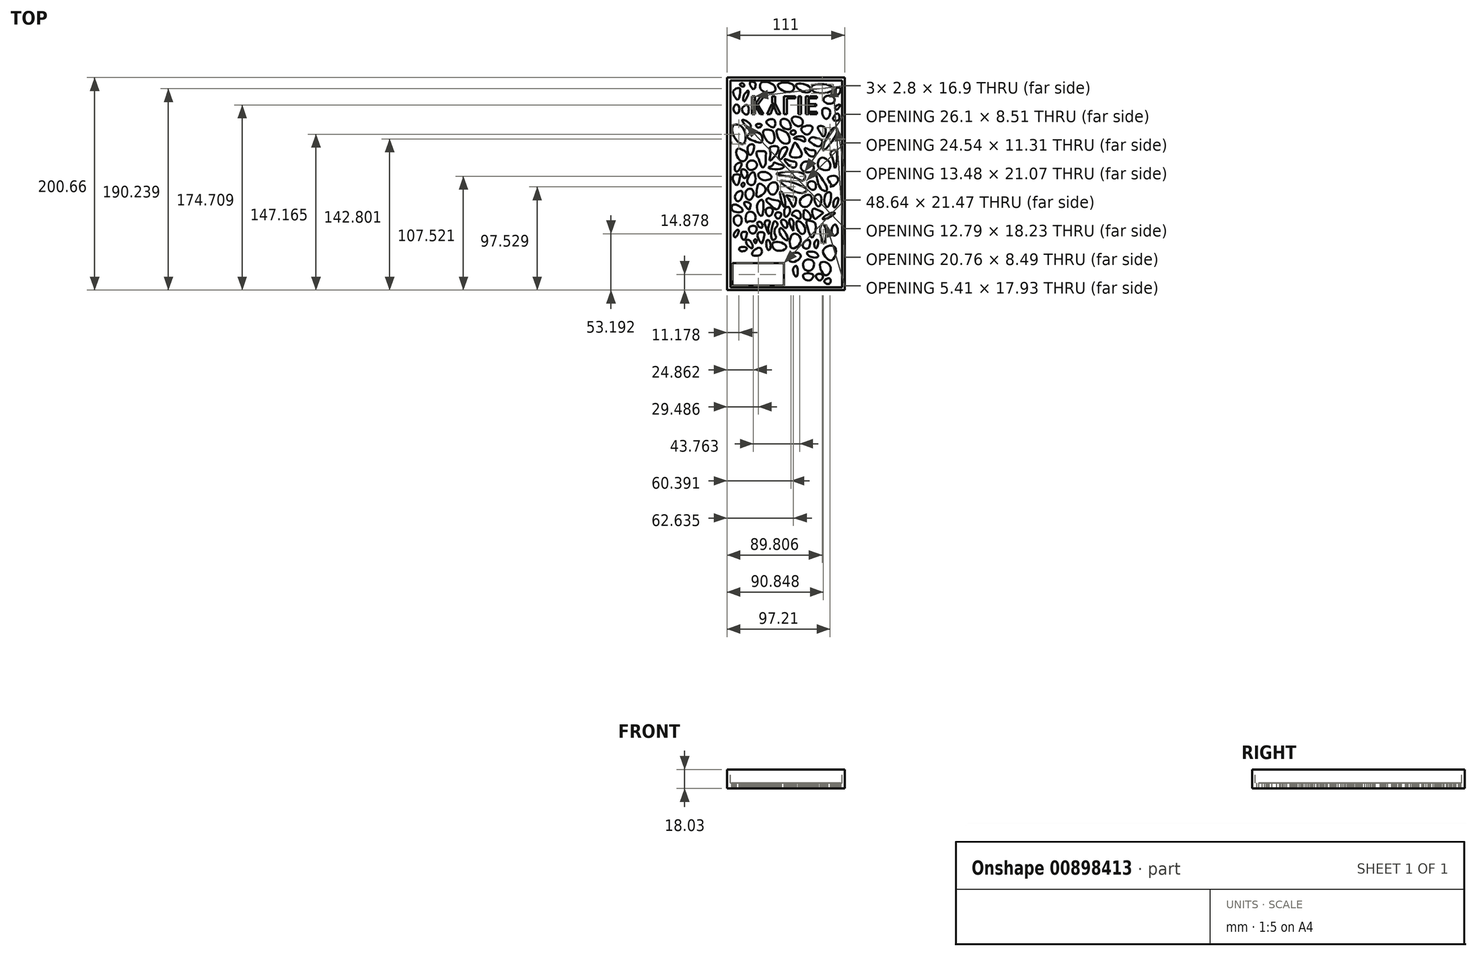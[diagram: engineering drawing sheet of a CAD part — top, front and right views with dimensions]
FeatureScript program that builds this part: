
annotation { "Feature Type Name" : "Feature", "Feature Type Description" : "" }
export const myFeature = defineFeature(function(context is Context, id is Id, definition is map)
    precondition{}
    {
        {
            var Q0;
            Q0=qCreatedBy(makeId("Top.planeOp"),FACE);
            var sketch = newSketch(context, id + "F0", { "sketchPlane" : qUnion([Q0])});
            skLineSegment(sketch, "E0.bottom", {"start": v(-57.32, 129.1) * mm, "end": v(53.68, 129.1) * mm});
            skLineSegment(sketch, "E0.top", {"start": v(-57.32, -71.56) * mm, "end": v(53.68, -71.56) * mm});
            skLineSegment(sketch, "E0.left", {"start": v(-57.32, 129.1) * mm, "end": v(-57.32, -71.56) * mm});
            skLineSegment(sketch, "E0.right", {"start": v(53.68, 129.1) * mm, "end": v(53.68, -71.56) * mm});
            skSolve(sketch);
        }
        {
            var Q0;
            Q0=makeQuery(id+"F0.imprint","IMPRINT",FACE,{"disambiguationData":[TD([[makeQuery(id+"F0.imprint","IMPRINT",EDGE,{"derivedFrom":sQuery(id+"F0.wireOp",EDGE,"E0.bottom")}),-1.0]])]});
            extrude(context, id + "F1", {"entities" : qUnion([Q0]), "depth" : 18.03 * mm, "offsetDistance" : 25.4 * mm});
        }
        {
            var Q0;
            Q0=makeQuery(id+"F1.opExtrude","CAP_FACE",FACE,{"disambiguationData":[OSD([sQuery(id+"F0.wireOp",EDGE,"E0.bottom"),sQuery(id+"F0.wireOp",EDGE,"E0.top"),sQuery(id+"F0.wireOp",EDGE,"E0.left"),sQuery(id+"F0.wireOp",EDGE,"E0.right")])],"isStart":false});
            var sketch = newSketch(context, id + "F2", { "sketchPlane" : qUnion([Q0])});
            skLineSegment(sketch, "E1.bottom", {"start": v(-54.27, 126.23) * mm, "end": v(51.3, 126.23) * mm});
            skLineSegment(sketch, "E1.top", {"start": v(-54.27, -68.92) * mm, "end": v(51.3, -68.92) * mm});
            skLineSegment(sketch, "E1.left", {"start": v(-54.27, 126.23) * mm, "end": v(-54.27, -68.92) * mm});
            skLineSegment(sketch, "E1.right", {"start": v(51.3, 126.23) * mm, "end": v(51.3, -68.92) * mm});
            skSolve(sketch);
        }
        {
            var Q0;
            Q0=makeQuery(id+"F2.imprint","IMPRINT",FACE,{"disambiguationData":[TD([[makeQuery(id+"F2.imprint","IMPRINT",EDGE,{"derivedFrom":sQuery(id+"F2.wireOp",EDGE,"E1.bottom")}),-1.0]])]});
            extrude(context, id + "F3", {"entities" : qUnion([Q0]), "operationType" : NewBodyOperationType.REMOVE, "oppositeDirection" : true, "depth" : 12.7 * mm, "offsetDistance" : 25.4 * mm});
        }
        {
            var Q0;
            Q0=makeQuery(id+"F1.opExtrude","CAP_FACE",FACE,{"disambiguationData":[OSD([sQuery(id+"F0.wireOp",EDGE,"E0.bottom"),sQuery(id+"F0.wireOp",EDGE,"E0.top"),sQuery(id+"F0.wireOp",EDGE,"E0.left"),sQuery(id+"F0.wireOp",EDGE,"E0.right")])],"isStart":true});
            var sketch = newSketch(context, id + "F4", { "sketchPlane" : qUnion([Q0])});
            skText(sketch, "E2", { "text": "KYLIE", "fontName": "AllertaStencil-Regular.ttf"});
            const initialGuessF4  = {"E2": [-0.03599, -0.1116, 1, 0, 0.01691]};
            skSetInitialGuess(sketch, initialGuessF4);
            skSolve(sketch);
        }
        {
            var Q0;
            Q0 = qSketchRegion(id + "F4", true);
            extrude(context, id + "F5", {"entities" : qUnion([Q0]), "operationType" : NewBodyOperationType.REMOVE, "oppositeDirection" : true, "depth" : 25.4 * mm, "offsetDistance" : 25.4 * mm});
        }
        {
            var Q0;
            Q0=makeQuery(id+"F1.opExtrude","CAP_FACE",FACE,{"disambiguationData":[OSD([sQuery(id+"F0.wireOp",EDGE,"E0.bottom"),sQuery(id+"F0.wireOp",EDGE,"E0.top"),sQuery(id+"F0.wireOp",EDGE,"E0.left"),sQuery(id+"F0.wireOp",EDGE,"E0.right")])],"isStart":true});
            var sketch = newSketch(context, id + "F6", { "sketchPlane" : qUnion([Q0])});
            skLineSegment(sketch, "E3.bottom", {"start": v(-52.16, 67.42) * mm, "end": v(-3.51, 67.42) * mm});
            skLineSegment(sketch, "E3.top", {"start": v(-52.16, 45.95) * mm, "end": v(-3.51, 45.95) * mm});
            skLineSegment(sketch, "E3.left", {"start": v(-52.16, 67.42) * mm, "end": v(-52.16, 45.95) * mm});
            skLineSegment(sketch, "E3.right", {"start": v(-3.51, 67.42) * mm, "end": v(-3.51, 45.95) * mm});
            skSolve(sketch);
        }
        {
            var Q0;
            Q0=makeQuery(id+"F6.imprint","IMPRINT",FACE,{"disambiguationData":[TD([[makeQuery(id+"F6.imprint","IMPRINT",EDGE,{"derivedFrom":sQuery(id+"F6.wireOp",EDGE,"E3.bottom")}),-1.0]])]});
            extrude(context, id + "F7", {"entities" : qUnion([Q0]), "operationType" : NewBodyOperationType.REMOVE, "oppositeDirection" : true, "depth" : 25.4 * mm, "offsetDistance" : 25.4 * mm});
        }
        {
            var Q0;
            Q0=makeQuery(id+"F1.opExtrude","CAP_FACE",FACE,{"disambiguationData":[OSD([sQuery(id+"F0.wireOp",EDGE,"E0.bottom"),sQuery(id+"F0.wireOp",EDGE,"E0.top"),sQuery(id+"F0.wireOp",EDGE,"E0.left"),sQuery(id+"F0.wireOp",EDGE,"E0.right")])],"isStart":true});
            var sketch = newSketch(context, id + "F8", { "sketchPlane" : qUnion([Q0])});
            skFitSpline(sketch, "E4", {"points": [v(-45.58, 33.96) * mm, v(-44.9, 31.22) * mm, v(-38.73, 31.9) * mm, v(-40.56, 34.41) * mm, v(-45.58, 33.96) * mm]});
            skFitSpline(sketch, "E5", {"points": [v(-33.47, 31.9) * mm, v(-38.73, 28.02) * mm, v(-38.73, 24.13) * mm, v(-35.07, 25.73) * mm, v(-33.47, 31.9) * mm]});
            skFitSpline(sketch, "E6", {"points": [v(-33.47, 38.07) * mm, v(-25.47, 37.84) * mm, v(-25.7, 31.9) * mm, v(-31.42, 33.73) * mm, v(-33.47, 38.07) * mm]});
            skFitSpline(sketch, "E7", {"points": [v(-33.47, 18.2) * mm, v(-36.67, 12.93) * mm, v(-30.73, 11.1) * mm, v(-29.59, 15.22) * mm, v(-33.47, 18.2) * mm]});
            skFitSpline(sketch, "E8", {"points": [v(-24.79, 27.33) * mm, v(-28.67, 19.79) * mm, v(-26.62, 17.05) * mm, v(-22.27, 17.73) * mm, v(-23.19, 24.13) * mm, v(-24.79, 27.33) * mm]});
            skFitSpline(sketch, "E9", {"points": [v(-30.5, 27.33) * mm, v(-31.64, 24.13) * mm, v(-29.59, 24.13) * mm, v(-30.5, 27.33) * mm]});
            skFitSpline(sketch, "E10", {"points": [v(-24.79, 12.7) * mm, v(-28.9, 8.14) * mm, v(-24.79, 7.9) * mm, v(-24.79, 12.7) * mm]});
            skFitSpline(sketch, "E11", {"points": [v(-41.47, 24.13) * mm, v(-43.98, 18.42) * mm, v(-40.78, 16.36) * mm, v(-38.73, 17.5) * mm, v(-41.47, 24.13) * mm]});
            skFitSpline(sketch, "E12", {"points": [v(-38.73, 7.68) * mm, v(-38.73, -0.78) * mm, v(-31.64, -0.78) * mm, v(-31.64, 6.3) * mm, v(-36.67, 6.54) * mm, v(-38.73, 7.68) * mm]});
            skFitSpline(sketch, "E13", {"points": [v(-17.7, 33.73) * mm, v(-20.22, 29.62) * mm, v(-19.08, 24.13) * mm, v(-16.33, 27.33) * mm, v(-17.7, 33.73) * mm]});
            skFitSpline(sketch, "E14", {"points": [v(-17.7, 18.65) * mm, v(-20.45, 12.93) * mm, v(-21.13, 6.3) * mm, v(-17.02, 6.3) * mm, v(-18.39, 12.7) * mm, v(-17.7, 18.65) * mm]});
            skFitSpline(sketch, "E15", {"points": [v(-14.28, 24.13) * mm, v(-14.96, 12.93) * mm, v(-12, 6.3) * mm, v(-9.48, 9.74) * mm, v(-11.53, 12.7) * mm, v(-12.22, 18.65) * mm, v(-11.08, 22.08) * mm, v(-14.28, 24.13) * mm]});
            skFitSpline(sketch, "E16", {"points": [v(-11.53, 33.73) * mm, v(-14.28, 27.33) * mm, v(-4.45, 27.33) * mm, v(-1.7, 31.9) * mm, v(-11.53, 33.73) * mm]});
            skFitSpline(sketch, "E17", {"points": [v(0.12, 24.13) * mm, v(-7.2, 18.65) * mm, v(-6.28, 12.93) * mm, v(0.12, 24.13) * mm]});
            skFitSpline(sketch, "E18", {"points": [v(3.78, 31.9) * mm, v(4.7, 18.65) * mm, v(12.23, 24.13) * mm, v(3.78, 31.9) * mm]});
            skFitSpline(sketch, "E19", {"points": [v(-1.7, 12.93) * mm, v(-6.28, 6.3) * mm, v(-1.7, 6.3) * mm, v(-1.7, 12.93) * mm]});
            skFitSpline(sketch, "E20", {"points": [v(5.15, 15.45) * mm, v(2.18, 9.96) * mm, v(2.18, 4.25) * mm, v(5.15, 6.3) * mm, v(5.15, 12.7) * mm, v(5.15, 15.45) * mm]});
            skFitSpline(sketch, "E21", {"points": [v(14.06, 29.62) * mm, v(19.32, 31.9) * mm, v(19.77, 24.13) * mm, v(14.06, 29.62) * mm]});
            skFitSpline(sketch, "E22", {"points": [v(14.29, 18.65) * mm, v(8.8, 12.7) * mm, v(9.26, 6.3) * mm, v(16.12, 12.7) * mm, v(14.29, 18.65) * mm]});
            skFitSpline(sketch, "E23", {"points": [v(23.2, 21.85) * mm, v(19.54, 15.45) * mm, v(17.94, 6.3) * mm, v(22.29, 6.3) * mm, v(26.4, 9.96) * mm, v(23.2, 21.85) * mm]});
            skFitSpline(sketch, "E24", {"points": [v(33.71, 27.33) * mm, v(31.43, 9.96) * mm, v(35.54, 12.7) * mm, v(33.71, 27.33) * mm]});
            skFitSpline(sketch, "E25", {"points": [v(27.09, 31.9) * mm, v(25.03, 27.33) * mm, v(28.23, 24.13) * mm, v(27.09, 31.9) * mm]});
            skFitSpline(sketch, "E26", {"points": [v(-24.79, 1.5) * mm, v(-29.13, -7.4) * mm, v(-24.79, -13.8) * mm, v(-23.19, -11.97) * mm, v(-24.79, 1.5) * mm]});
            skFitSpline(sketch, "E27", {"points": [v(-17.7, 1.74) * mm, v(-20.45, -4.89) * mm, v(-14.28, -4.89) * mm, v(-17.7, 1.74) * mm]});
            skFitSpline(sketch, "E28", {"points": [v(-9.25, 4.02) * mm, v(-11.53, -0.78) * mm, v(-6.28, -0.78) * mm, v(-9.25, 4.02) * mm]});
            skFitSpline(sketch, "E29", {"points": [v(-1.48, 2.42) * mm, v(-3.3, -1.23) * mm, v(-1.25, -6.95) * mm, v(2.18, -4.89) * mm, v(-1.48, 2.42) * mm]});
            skFitSpline(sketch, "E30", {"points": [v(-9.93, -4.89) * mm, v(-16.8, -9.23) * mm, v(-20.22, -12.66) * mm, v(-19.08, -15.17) * mm, v(-14.05, -13.8) * mm, v(-7.42, -11.52) * mm, v(-9.93, -4.89) * mm]});
            skFitSpline(sketch, "E31", {"points": [v(-3.3, -6.95) * mm, v(-3.3, -16.54) * mm, v(-7.2, -21.34) * mm, v(-3.3, -6.95) * mm]});
            skFitSpline(sketch, "E32", {"points": [v(6.52, 1.74) * mm, v(11.09, 4.25) * mm, v(11.77, -1.23) * mm, v(6.52, -3.3) * mm, v(4, 0.6) * mm, v(6.52, 1.74) * mm]});
            skFitSpline(sketch, "E33", {"points": [v(15.66, 4.25) * mm, v(21.14, 4.25) * mm, v(20.23, -1.23) * mm, v(15.66, -4.2) * mm, v(14.97, -1.23) * mm, v(15.66, 4.25) * mm]});
            skFitSpline(sketch, "E34", {"points": [v(25.49, 4.25) * mm, v(23.43, -4.66) * mm, v(28.91, -3.98) * mm, v(33.26, -1.23) * mm, v(29.6, 1.5) * mm, v(25.49, 4.25) * mm]});
            skFitSpline(sketch, "E35", {"points": [v(36, 4.25) * mm, v(33.03, 4.25) * mm, v(40.34, -1.23) * mm, v(44.45, -1.23) * mm, v(36, 4.25) * mm]});
            skFitSpline(sketch, "E36", {"points": [v(5.38, -6.95) * mm, v(2.18, -12.43) * mm, v(-1.25, -17.92) * mm, v(4, -16.77) * mm, v(7.66, -15.63) * mm, v(5.38, -6.95) * mm]});
            skFitSpline(sketch, "E37", {"points": [v(-37.13, -13.8) * mm, v(-39.87, -20.89) * mm, v(-34.39, -24.09) * mm, v(-32.56, -17.46) * mm, v(-37.13, -13.8) * mm]});
            skFitSpline(sketch, "E38", {"points": [v(-35.99, -4.66) * mm, v(-39.41, -6.95) * mm, v(-40.78, -11.52) * mm, v(-35.3, -9.92) * mm, v(-35.53, -6.95) * mm, v(-35.99, -4.66) * mm]});
            skFitSpline(sketch, "E39", {"points": [v(-28.67, -16.54) * mm, v(-20.9, -23.17) * mm, v(-26.85, -28.88) * mm, v(-29.13, -23.4) * mm, v(-28.67, -16.54) * mm]});
            skFitSpline(sketch, "E40", {"points": [v(-14.73, -18.6) * mm, v(-18.62, -26.14) * mm, v(-11.53, -30.03) * mm, v(-9.7, -23.17) * mm, v(-14.73, -18.6) * mm]});
            skFitSpline(sketch, "E41", {"points": [v(14.06, -7.4) * mm, v(11.77, -13.8) * mm, v(21.14, -18.14) * mm, v(21.14, -9.92) * mm, v(14.06, -7.4) * mm]});
            skFitSpline(sketch, "E42", {"points": [v(29.14, -7.4) * mm, v(25.49, -16.54) * mm, v(30.97, -17.69) * mm, v(29.14, -7.4) * mm]});
            skFitSpline(sketch, "E43", {"points": [v(37.37, -6.95) * mm, v(35.08, -17.69) * mm, v(40.34, -20.2) * mm, v(37.37, -6.95) * mm]});
            skFitSpline(sketch, "E44", {"points": [v(-1.25, -26.14) * mm, v(13.6, -19.97) * mm, v(17.94, -23.17) * mm, v(11.09, -27.51) * mm, v(2.18, -30.71) * mm, v(-6.96, -31.4) * mm, v(-1.25, -26.14) * mm]});
            skFitSpline(sketch, "E45", {"points": [v(24.8, -23.17) * mm, v(18.63, -28.43) * mm, v(25.03, -30.71) * mm, v(24.8, -23.17) * mm]});
            skFitSpline(sketch, "E46", {"points": [v(32.34, -23.17) * mm, v(37.14, -23.17) * mm, v(27.09, -39.4) * mm, v(27.77, -33.23) * mm, v(32.34, -23.17) * mm]});
            skFitSpline(sketch, "E47", {"points": [v(8.12, -34.14) * mm, v(14.52, -31.86) * mm, v(15.43, -38.03) * mm, v(-10.62, -38.25) * mm, v(8.12, -34.14) * mm]});
            skFitSpline(sketch, "E48", {"points": [v(-24.79, -33) * mm, v(-15.65, -34.14) * mm, v(-19.08, -39.17) * mm, v(-27.53, -38.48) * mm, v(-24.79, -33) * mm]});
            skFitSpline(sketch, "E49", {"points": [v(-37.36, -28.88) * mm, v(-31.64, -28.88) * mm, v(-32.1, -39.62) * mm, v(-37.13, -35.28) * mm, v(-37.36, -28.88) * mm]});
            skFitSpline(sketch, "E50", {"points": [v(-36.21, -42.14) * mm, v(-38.27, -48.3) * mm, v(-32.1, -50.6) * mm, v(-29.13, -45.34) * mm, v(-36.21, -42.14) * mm]});
            skFitSpline(sketch, "E51", {"points": [v(-23.87, -44.2) * mm, v(-27.3, -51.74) * mm, v(-29.13, -55.4) * mm, v(-29.13, -59.28) * mm, v(-24.79, -59.73) * mm, v(-20.9, -58.82) * mm, v(-20.9, -52.88) * mm, v(-20.9, -48.08) * mm, v(-23.87, -44.2) * mm]});
            skFitSpline(sketch, "E52", {"points": [v(-18.39, -44.42) * mm, v(-10.16, -42.37) * mm, v(-3.3, -45.34) * mm, v(-8.8, -47.62) * mm, v(-13.13, -48.77) * mm, v(-14.5, -46.02) * mm, v(-18.39, -44.42) * mm]});
            skFitSpline(sketch, "E53", {"points": [v(-17.02, -50.82) * mm, v(-10.62, -57.22) * mm, v(-9.7, -63.85) * mm, v(-16.8, -63.4) * mm, v(-16.33, -57.68) * mm, v(-17.02, -50.82) * mm]});
            skFitSpline(sketch, "E54", {"points": [v(1.95, -45.57) * mm, v(7.2, -44.65) * mm, v(7.89, -48.77) * mm, v(2.18, -50.6) * mm, v(-3.08, -51.96) * mm, v(1.95, -45.57) * mm]});
            skFitSpline(sketch, "E55", {"points": [v(-7.65, -51.74) * mm, v(-1.02, -59.73) * mm, v(-1.02, -63.16) * mm, v(-6.05, -61.56) * mm, v(-7.65, -51.74) * mm]});
            skFitSpline(sketch, "E56", {"points": [v(13.37, -41.9) * mm, v(23.66, -41) * mm, v(22.97, -47.62) * mm, v(14.52, -49) * mm, v(13.37, -41.9) * mm]});
            skFitSpline(sketch, "E57", {"points": [v(30.51, -43.28) * mm, v(38.05, -41.9) * mm, v(40.11, -44.65) * mm, v(39.43, -49.22) * mm, v(31.88, -53.56) * mm, v(28.46, -47.62) * mm, v(30.51, -43.28) * mm]});
            skFitSpline(sketch, "E58", {"points": [v(25.03, -54.94) * mm, v(18.86, -56.76) * mm, v(16.12, -62.48) * mm, v(20.92, -60.88) * mm, v(25.71, -59.96) * mm, v(25.03, -54.94) * mm]});
            skFitSpline(sketch, "E59", {"points": [v(2.86, -54.7) * mm, v(12.92, -55.16) * mm, v(9.95, -63.85) * mm, v(6.75, -67.73) * mm, v(4, -62.25) * mm, v(2.86, -54.7) * mm]});
            skFitSpline(sketch, "E60", {"points": [v(-31.42, -69.1) * mm, v(-24.79, -68.19) * mm, v(-24.79, -74.59) * mm, v(-33.24, -77.33) * mm, v(-38.27, -73.22) * mm, v(-31.42, -69.1) * mm]});
            skFitSpline(sketch, "E61", {"points": [v(-35.3, -56.08) * mm, v(-37.59, -63.85) * mm, v(-32.1, -65.45) * mm, v(-35.3, -56.08) * mm]});
            skFitSpline(sketch, "E62", {"points": [v(-17.93, -67.96) * mm, v(-22.96, -78.7) * mm, v(-15.65, -79.39) * mm, v(-12.9, -75.73) * mm, v(-13.6, -68.19) * mm, v(-17.93, -67.96) * mm]});
            skFitSpline(sketch, "E63", {"points": [v(-7.2, -69.56) * mm, v(-9.93, -80.07) * mm, v(-5.36, -79.39) * mm, v(0.12, -75.73) * mm, v(1.03, -67.5) * mm, v(-7.2, -69.56) * mm]});
            skFitSpline(sketch, "E64", {"points": [v(3.1, -78.47) * mm, v(7.2, -78.7) * mm, v(6.52, -75.73) * mm, v(3.55, -75.73) * mm, v(3.1, -78.47) * mm]});
            skFitSpline(sketch, "E65", {"points": [v(5.83, -71.85) * mm, v(14.29, -73.45) * mm, v(16.34, -69.1) * mm, v(10.63, -70.7) * mm, v(5.83, -71.85) * mm]});
            skFitSpline(sketch, "E66", {"points": [v(22.97, -67.05) * mm, v(29.6, -64.3) * mm, v(32.57, -69.56) * mm, v(26.17, -72.3) * mm, v(22.97, -72.76) * mm, v(20, -69.56) * mm, v(22.97, -67.05) * mm]});
            skFitSpline(sketch, "E67", {"points": [v(14.29, -77.56) * mm, v(13.15, -81.67) * mm, v(22.97, -82.81) * mm, v(19.54, -75.73) * mm, v(14.29, -77.56) * mm]});
            skFitSpline(sketch, "E68", {"points": [v(30.06, -78.24) * mm, v(28.68, -82.81) * mm, v(34.85, -81.9) * mm, v(34.17, -73.67) * mm, v(30.06, -78.24) * mm]});
            skFitSpline(sketch, "E69", {"points": [v(-18.62, -84.64) * mm, v(-12.9, -82.59) * mm, v(-12.9, -89.21) * mm, v(-19.99, -88.07) * mm, v(-18.62, -84.64) * mm]});
            skFitSpline(sketch, "E70", {"points": [v(-5.6, -83.04) * mm, v(2.18, -80.76) * mm, v(0.58, -88.3) * mm, v(-5.82, -89.44) * mm, v(-5.6, -83.04) * mm]});
            skFitSpline(sketch, "E71", {"points": [v(8.12, -83.73) * mm, v(13.6, -84.87) * mm, v(12.69, -90.58) * mm, v(4, -91.04) * mm, v(8.12, -83.73) * mm]});
            skFitSpline(sketch, "E72", {"points": [v(-32.33, -118.23) * mm, v(-35.76, -124.4) * mm, v(-31.42, -124.63) * mm, v(-30.5, -121.43) * mm, v(-32.33, -118.23) * mm]});
            skFitSpline(sketch, "E73", {"points": [v(-24.79, -117.32) * mm, v(-24.79, -124.4) * mm, v(-12.9, -121.66) * mm, v(-12.9, -115.72) * mm, v(-24.79, -117.32) * mm]});
            skFitSpline(sketch, "E74", {"points": [v(-3.3, -116.18) * mm, v(-9.25, -122.58) * mm, v(4, -123.03) * mm, v(5.15, -117.32) * mm, v(-3.3, -116.18) * mm]});
            skFitSpline(sketch, "E75", {"points": [v(11.32, -117.32) * mm, v(8.12, -122.8) * mm, v(20.23, -120.75) * mm, v(20.69, -115.72) * mm, v(11.32, -117.32) * mm]});
            skFitSpline(sketch, "E76", {"points": [v(24.8, -115.72) * mm, v(22.97, -121.2) * mm, v(41.02, -120.98) * mm, v(42.17, -117.1) * mm, v(24.8, -115.72) * mm]});
            skFitSpline(sketch, "E77", {"points": [v(-39.18, -82.81) * mm, v(-42.84, -89.21) * mm, v(-35.07, -84.41) * mm, v(-36.44, -80.99) * mm, v(-39.18, -82.81) * mm]});
            skFitSpline(sketch, "E78", {"points": [v(-40.78, -94.93) * mm, v(-43.07, -99.95) * mm, v(-38.04, -102.92) * mm, v(-37.81, -94.7) * mm, v(-40.78, -94.93) * mm]});
            skFitSpline(sketch, "E79", {"points": [v(-41.47, -106.8) * mm, v(-41.7, -111.6) * mm, v(-37.13, -116.63) * mm, v(-39.41, -108.64) * mm, v(-41.47, -106.8) * mm]});
            skFitSpline(sketch, "E80", {"points": [v(34.17, -91.5) * mm, v(33.26, -99.5) * mm, v(39.65, -98.35) * mm, v(37.6, -90.58) * mm, v(34.17, -91.5) * mm]});
            skFitSpline(sketch, "E81", {"points": [v(36.45, -104.98) * mm, v(33.94, -109.55) * mm, v(41.71, -111.6) * mm, v(43.77, -106.12) * mm, v(36.45, -104.98) * mm]});
            skFitSpline(sketch, "E82", {"points": [v(1.06, 39.94) * mm, v(8.37, 36.12) * mm, v(12.23, 39.75) * mm, v(3.78, 44.94) * mm, v(1.06, 39.94) * mm]});
            skFitSpline(sketch, "E83", {"points": [v(21.41, 39.94) * mm, v(18.28, 36.12) * mm, v(26.24, 36.12) * mm, v(28.53, 39.94) * mm, v(21.41, 39.94) * mm]});
            skFitSpline(sketch, "E84", {"points": [v(36.53, 41.36) * mm, v(33.99, 32.67) * mm, v(44.2, 30.7) * mm, v(42.62, 42.6) * mm, v(36.53, 41.36) * mm]});
            skFitSpline(sketch, "E85", {"points": [v(16.06, 52.05) * mm, v(15.75, 44.07) * mm, v(23.43, 43.84) * mm, v(23.35, 51.6) * mm, v(16.06, 52.05) * mm]});
            skFitSpline(sketch, "E86", {"points": [v(8.37, 58.55) * mm, v(5, 52.26) * mm, v(8.37, 48.98) * mm, v(8.37, 58.55) * mm]});
            skFitSpline(sketch, "E87", {"points": [v(19.46, 62.5) * mm, v(14.54, 57.21) * mm, v(23.96, 57.15) * mm, v(19.46, 62.5) * mm]});
            skFitSpline(sketch, "E88", {"points": [v(35.52, 57.48) * mm, v(30.6, 46.46) * mm, v(37.18, 45.88) * mm, v(40.5, 52.65) * mm, v(35.52, 57.48) * mm]});
            skFitSpline(sketch, "E89", {"points": [v(-45.54, 10.28) * mm, v(-50.01, 8.76) * mm, v(-49.97, 2.2) * mm, v(-44.18, 2.12) * mm, v(-45.54, 10.28) * mm]});
            skFitSpline(sketch, "E90", {"points": [v(-49.37, 21.63) * mm, v(-50.75, 18.36) * mm, v(-46.4, 14.82) * mm, v(-49.37, 21.63) * mm]});
            skFitSpline(sketch, "E91", {"points": [v(-46.3, -12.35) * mm, v(-49.7, -17.67) * mm, v(-43.27, -21.63) * mm, v(-46.3, -12.35) * mm]});
            skFitSpline(sketch, "E92", {"points": [v(-51.6, -3.23) * mm, v(-52.5, -8.26) * mm, v(-46.71, -8.35) * mm, v(-42.7, -3.01) * mm, v(-51.6, -3.23) * mm]});
            skFitSpline(sketch, "E93", {"points": [v(-48.24, -27.5) * mm, v(-51.67, -36.28) * mm, v(-45.13, -37.2) * mm, v(-44.99, -35.4) * mm, v(-48.24, -27.5) * mm]});
            skFitSpline(sketch, "E94", {"points": [v(-41.06, -34.33) * mm, v(-43.6, -42.15) * mm, v(-38.27, -39.6) * mm, v(-41.06, -34.33) * mm]});
            skFitSpline(sketch, "E95", {"points": [v(-42.55, -25.92) * mm, v(-43.45, -28.92) * mm, v(-40.94, -29.26) * mm, v(-42.55, -25.92) * mm]});
            skFitSpline(sketch, "E96", {"points": [v(-48.04, -40.22) * mm, v(-49.54, -45.9) * mm, v(-43.94, -48.3) * mm, v(-48.04, -40.22) * mm]});
            skFitSpline(sketch, "E97", {"points": [v(-41.57, -50.1) * mm, v(-47.73, -54.6) * mm, v(-47.49, -61.81) * mm, v(-42.58, -60.82) * mm, v(-38.27, -56.74) * mm, v(-41.57, -50.1) * mm]});
            skFitSpline(sketch, "E98", {"points": [v(-42.07, -66.49) * mm, v(-51.59, -75.5) * mm, v(-50.5, -84.6) * mm, v(-41.3, -79.99) * mm, v(-42.07, -66.49) * mm]});
            skFitSpline(sketch, "E99", {"points": [v(-27.32, -81.98) * mm, v(-29.93, -84.64) * mm, v(-24.79, -84.64) * mm, v(-27.32, -81.98) * mm]});
            skFitSpline(sketch, "E100", {"points": [v(43.31, 20.13) * mm, v(41.51, 13.82) * mm, v(44.65, 9.59) * mm, v(46.76, 12.61) * mm, v(46.83, 17.97) * mm, v(43.31, 20.13) * mm]});
            skFitSpline(sketch, "E101", {"points": [v(44.41, -6.64) * mm, v(43.34, -12.22) * mm, v(47.57, -15.27) * mm, v(44.41, -6.64) * mm]});
            skFitSpline(sketch, "E102", {"points": [v(39.44, 65.4) * mm, v(34.5, 63.32) * mm, v(39.42, 60.52) * mm, v(39.44, 65.4) * mm]});
            skFitSpline(sketch, "E103", {"points": [v(30.18, 62.48) * mm, v(26.64, 58.14) * mm, v(28.72, 56.3) * mm, v(33.13, 57.94) * mm, v(30.18, 62.48) * mm]});
            skFitSpline(sketch, "E104", {"points": [v(41.24, -27.59) * mm, v(37.77, -34.15) * mm, v(46.13, -35.75) * mm, v(46, -29.25) * mm, v(40.23, -26.05) * mm, v(41.24, -27.59) * mm]});
            skFitSpline(sketch, "E105", {"points": [v(44.65, -43.6) * mm, v(42.24, -53.3) * mm, v(40.22, -58.12) * mm, v(44.65, -60.76) * mm, v(46.5, -55.08) * mm, v(44.65, -43.6) * mm]});
            skFitSpline(sketch, "E106", {"points": [v(33.15, -60.7) * mm, v(41.33, -68.42) * mm, v(46.55, -80.49) * mm, v(42.74, -81.22) * mm, v(33.15, -60.7) * mm]});
            skFitSpline(sketch, "E107", {"points": [v(43.42, -88.94) * mm, v(43.15, -91.7) * mm, v(47.18, -95.15) * mm, v(48.23, -89.54) * mm, v(43.42, -88.94) * mm]});
            skFitSpline(sketch, "E108", {"points": [v(45.61, -98.86) * mm, v(44.88, -101.38) * mm, v(49.12, -103.54) * mm, v(47.58, -99.83) * mm, v(45.61, -98.86) * mm]});
            skFitSpline(sketch, "E109", {"points": [v(46.5, -112.85) * mm, v(45.58, -118.64) * mm, v(49.44, -119.1) * mm, v(48.85, -114.55) * mm, v(46.5, -112.85) * mm]});
            skFitSpline(sketch, "E110", {"points": [v(-47.43, -95.45) * mm, v(-51.23, -98.8) * mm, v(-48.73, -103.65) * mm, v(-45.9, -101.3) * mm, v(-47.43, -95.45) * mm]});
            skFitSpline(sketch, "E111", {"points": [v(-47.19, -108.35) * mm, v(-50.59, -112.26) * mm, v(-51, -116.98) * mm, v(-45.97, -119.27) * mm, v(-44.93, -115.8) * mm, v(-47.19, -108.35) * mm]});
            skFitSpline(sketch, "E112", {"points": [v(-41.45, -120.65) * mm, v(-45.18, -122.53) * mm, v(-42.06, -123.52) * mm, v(-41.45, -120.65) * mm]});
            skSolve(sketch);
        }
        {
            var Q0;
            Q0 = qSketchRegion(id + "F8", true);
            extrude(context, id + "F9", {"entities" : qUnion([Q0]), "operationType" : NewBodyOperationType.REMOVE, "oppositeDirection" : true, "depth" : 25.4 * mm, "offsetDistance" : 25.4 * mm});
        }
    });
